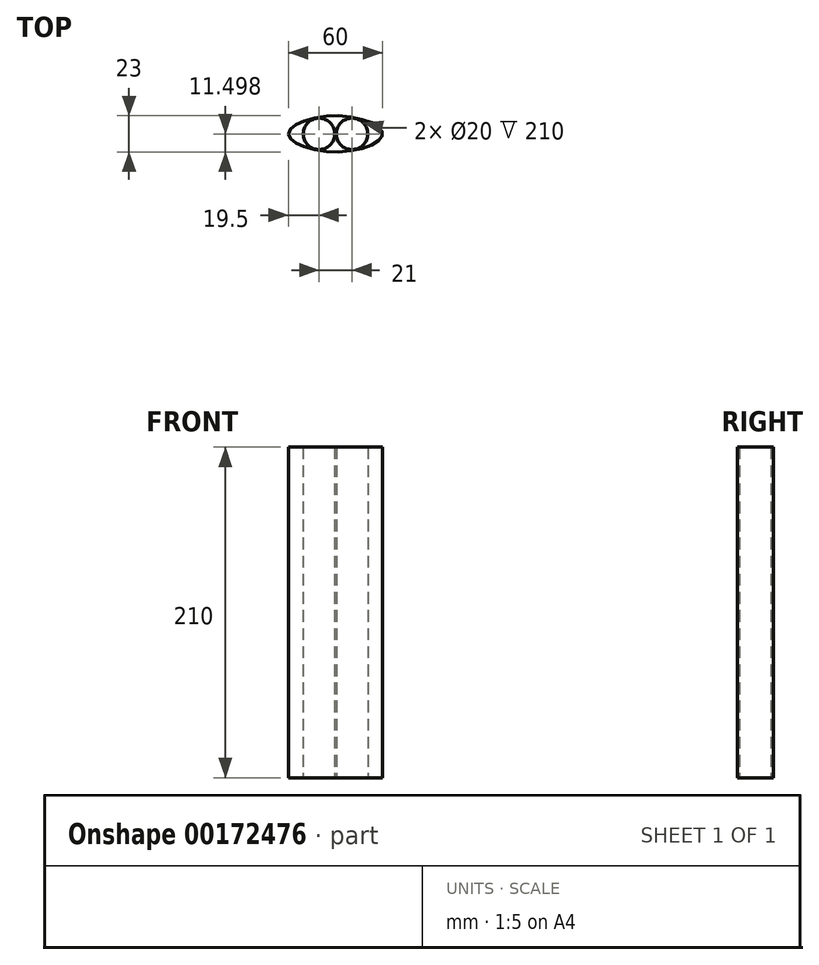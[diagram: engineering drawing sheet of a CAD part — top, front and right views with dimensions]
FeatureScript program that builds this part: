
annotation { "Feature Type Name" : "Feature", "Feature Type Description" : "" }
export const myFeature = defineFeature(function(context is Context, id is Id, definition is map)
    precondition{}
    {
        {
            var Q0;
            Q0=qCreatedBy(makeId("Top.planeOp"),FACE);
            var sketch = newSketch(context, id + "F0", { "sketchPlane" : qUnion([Q0])});
            skLineSegment(sketch, "E0", {"start": v(0, 11.51) * mm, "end": v(0, -11.49) * mm, "construction": true});
            skLineSegment(sketch, "E1", {"start": v(-60, 0) * mm, "end": v(0, 0.01) * mm, "construction": true});
            skPoint(sketch, "E1.endSnap0", {"position": v(0, 0.01) * mm});
            skPoint(sketch, "E2", {"position": v(-30, 11.51) * mm});
            skPoint(sketch, "E2.positionSnap0", {"position": v(-30, 0) * mm});
            skPoint(sketch, "E3", {"position": v(-30, -11.49) * mm});
            skFitSpline(sketch, "E4", {"points": [v(-60, 0) * mm, v(-30, 11.51) * mm, v(0, 0.01) * mm, v(-30, -11.49) * mm, v(-60, 0) * mm]});
            skLineSegment(sketch, "E5", {"start": v(-30, 5.69) * mm, "end": v(-9, 5.7) * mm, "construction": true});
            skLineSegment(sketch, "E6", {"start": v(7.32, 0) * mm, "end": v(7.32, 10) * mm, "construction": true});
            skLineSegment(sketch, "E7", {"start": v(7.32, 10) * mm, "end": v(-30, 10) * mm, "construction": true});
            skCircle(sketch, "E8", {"center": v(-19.5, 0) * mm, "radius": 10 * mm});
            skPoint(sketch, "E8.centerSnap0", {"position": v(-19.5, 5.7) * mm});
            skLineSegment(sketch, "E9", {"start": v(-30, 11.51) * mm, "end": v(-30, -11.49) * mm, "construction": true});
            skCircle(sketch, "E10.MirrorC", {"center": v(-40.5, 0) * mm, "radius": 10 * mm});
            skSolve(sketch);
        }
        {
            var Q0;
            Q0 = qSketchRegion(id + "F0", true);
            extrude(context, id + "F1", {"entities" : qUnion([Q0]), "depth" : 210 * mm});
        }
    });
